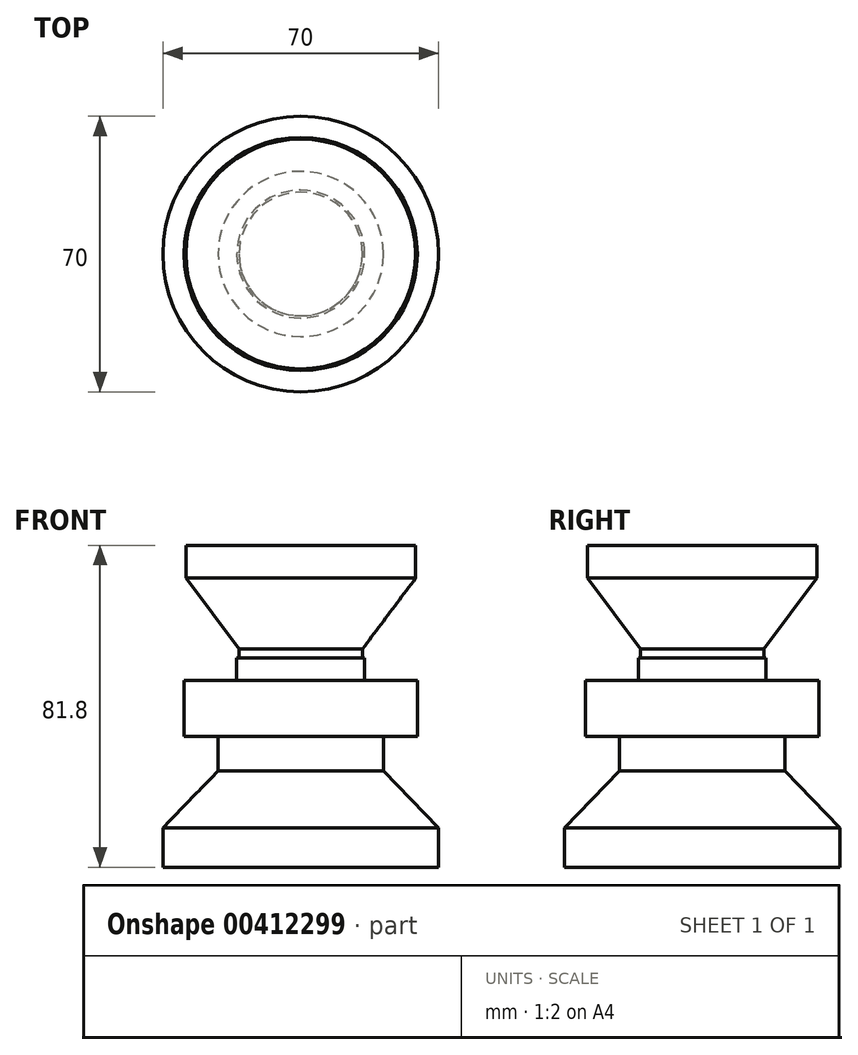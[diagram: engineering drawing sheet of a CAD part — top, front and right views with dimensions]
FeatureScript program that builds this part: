
annotation { "Feature Type Name" : "Feature", "Feature Type Description" : "" }
export const myFeature = defineFeature(function(context is Context, id is Id, definition is map)
    precondition{}
    {
        {
            var Q0;
            Q0=qCreatedBy(makeId("Top.planeOp"),FACE);
            var sketch = newSketch(context, id + "F0", { "sketchPlane" : qUnion([Q0])});
            skCircle(sketch, "E0", {"center": v(0, 0) * mm, "radius": 29.18 * mm});
            skSolve(sketch);
        }
        {
            var Q0;
            Q0 = qSketchRegion(id + "F0", true);
            extrude(context, id + "F1", {"entities" : qUnion([Q0]), "depth" : 8.35 * mm});
        }
        {
            var Q0;
            Q0=makeQuery(id+"F1.opExtrude","CAP_FACE",FACE,{"disambiguationData":[OSD([sQuery(id+"F0.wireOp",EDGE,"E0")])],"isStart":true});
            cPlane(context, id + "F2", {"entities" : qUnion([Q0]), "cplaneType" : CPlaneType.OFFSET, "offset" : 18 * mm, "width" : 150 * mm, "height" : 150 * mm});
        }
        {
            var Q0;
            Q0=qCreatedBy(id+"F2.planeOp",FACE);
            var sketch = newSketch(context, id + "F3", { "sketchPlane" : qUnion([Q0])});
            skCircle(sketch, "E1", {"center": v(0, 0) * mm, "radius": 15.69 * mm});
            skSolve(sketch);
        }
        {
            var Q1;
            Q1=makeQuery(id+"F1.opExtrude","CAP_FACE",FACE,{"disambiguationData":[OSD([sQuery(id+"F0.wireOp",EDGE,"E0")])],"isStart":true});
            var Q2;
            Q2=makeQuery(id+"F3.imprint","IMPRINT",FACE,{"disambiguationData":[TD([[makeQuery(id+"F3.imprint","IMPRINT",EDGE,{"derivedFrom":sQuery(id+"F3.wireOp",EDGE,"E1")}),1.0]])]});
            loft(context, id + "F4", {"operationType" : NewBodyOperationType.ADD, "sheetProfilesArray" : [{ "sheetProfileEntities" : qUnion([Q1]) }, { "sheetProfileEntities" : qUnion([Q2]) }]});
        }
        {
            var Q0;
            Q0=makeQuery(id+"F4.opLoft","CAP_FACE",FACE,{"disambiguationData":[OSD([makeQuery(id+"F3.imprint","IMPRINT",FACE,{"disambiguationData":[TD([[makeQuery(id+"F3.imprint","IMPRINT",EDGE,{"derivedFrom":sQuery(id+"F3.wireOp",EDGE,"E1")}),1.0]])]})])],"isStart":true});
            var sketch = newSketch(context, id + "F5", { "sketchPlane" : qUnion([Q0])});
            skCircle(sketch, "E2", {"center": v(0, 0) * mm, "radius": 15.69 * mm});
            skSolve(sketch);
        }
        {
            var Q0;
            Q0 = qSketchRegion(id + "F5", true);
            extrude(context, id + "F6", {"entities" : qUnion([Q0]), "operationType" : NewBodyOperationType.ADD, "depth" : 2.25 * mm});
        }
        {
            var Q0;
            Q0=makeQuery(id+"F6.opExtrude","CAP_FACE",FACE,{"disambiguationData":[OSD([sQuery(id+"F5.wireOp",EDGE,"E2")])],"isStart":false});
            var sketch = newSketch(context, id + "F7", { "sketchPlane" : qUnion([Q0])});
            skCircle(sketch, "E3", {"center": v(0, 0) * mm, "radius": 16.25 * mm});
            skSolve(sketch);
        }
        {
            var Q0;
            Q0 = qSketchRegion(id + "F7", true);
            extrude(context, id + "F8", {"entities" : qUnion([Q0]), "operationType" : NewBodyOperationType.ADD, "depth" : 5.75 * mm});
        }
        {
            var Q0;
            Q0=makeQuery(id+"F8.opExtrude","CAP_FACE",FACE,{"disambiguationData":[OSD([sQuery(id+"F7.wireOp",EDGE,"E3")])],"isStart":false});
            var sketch = newSketch(context, id + "F9", { "sketchPlane" : qUnion([Q0])});
            skCircle(sketch, "E4", {"center": v(0, 0) * mm, "radius": 29.63 * mm});
            skSolve(sketch);
        }
        {
            var Q0;
            Q0 = qSketchRegion(id + "F9", true);
            extrude(context, id + "F10", {"entities" : qUnion([Q0]), "operationType" : NewBodyOperationType.ADD, "depth" : 14.2 * mm});
        }
        {
            var Q0;
            Q0=makeQuery(id+"F10.opExtrude","CAP_FACE",FACE,{"disambiguationData":[OSD([sQuery(id+"F9.wireOp",EDGE,"E4")])],"isStart":false});
            var sketch = newSketch(context, id + "F11", { "sketchPlane" : qUnion([Q0])});
            skCircle(sketch, "E5", {"center": v(0, 0) * mm, "radius": 21 * mm});
            skSolve(sketch);
        }
        {
            var Q0;
            Q0 = qSketchRegion(id + "F11", true);
            extrude(context, id + "F12", {"entities" : qUnion([Q0]), "operationType" : NewBodyOperationType.ADD, "depth" : 8.75 * mm});
        }
        {
            var Q0;
            Q0=makeQuery(id+"F12.opExtrude","CAP_FACE",FACE,{"disambiguationData":[OSD([sQuery(id+"F11.wireOp",EDGE,"E5")])],"isStart":false});
            cPlane(context, id + "F13", {"entities" : qUnion([Q0]), "cplaneType" : CPlaneType.OFFSET, "offset" : 14.5 * mm, "width" : 150 * mm, "height" : 150 * mm});
        }
        {
            var Q0;
            Q0=qCreatedBy(id+"F13.planeOp",FACE);
            var sketch = newSketch(context, id + "F14", { "sketchPlane" : qUnion([Q0])});
            skCircle(sketch, "E6", {"center": v(0, 0) * mm, "radius": 35 * mm});
            skSolve(sketch);
        }
        {
            var Q1;
            Q1=makeQuery(id+"F12.opExtrude","CAP_FACE",FACE,{"disambiguationData":[OSD([sQuery(id+"F11.wireOp",EDGE,"E5")])],"isStart":false});
            var Q2;
            Q2=makeQuery(id+"F14.imprint","IMPRINT",FACE,{"disambiguationData":[TD([[makeQuery(id+"F14.imprint","IMPRINT",EDGE,{"derivedFrom":sQuery(id+"F14.wireOp",EDGE,"E6")}),1.0]])]});
            loft(context, id + "F15", {"operationType" : NewBodyOperationType.ADD, "sheetProfilesArray" : [{ "sheetProfileEntities" : qUnion([Q1]) }, { "sheetProfileEntities" : qUnion([Q2]) }]});
        }
        {
            var Q0;
            Q0=makeQuery(id+"F15.opLoft","CAP_FACE",FACE,{"disambiguationData":[OSD([makeQuery(id+"F14.imprint","IMPRINT",FACE,{"disambiguationData":[TD([[makeQuery(id+"F14.imprint","IMPRINT",EDGE,{"derivedFrom":sQuery(id+"F14.wireOp",EDGE,"E6")}),1.0]])]})])],"isStart":true});
            var sketch = newSketch(context, id + "F16", { "sketchPlane" : qUnion([Q0])});
            skCircle(sketch, "E7", {"center": v(0, 0) * mm, "radius": 35 * mm});
            skSolve(sketch);
        }
        {
            var Q0;
            Q0 = qSketchRegion(id + "F16", true);
            extrude(context, id + "F17", {"entities" : qUnion([Q0]), "operationType" : NewBodyOperationType.ADD, "depth" : 10 * mm});
        }
    });
